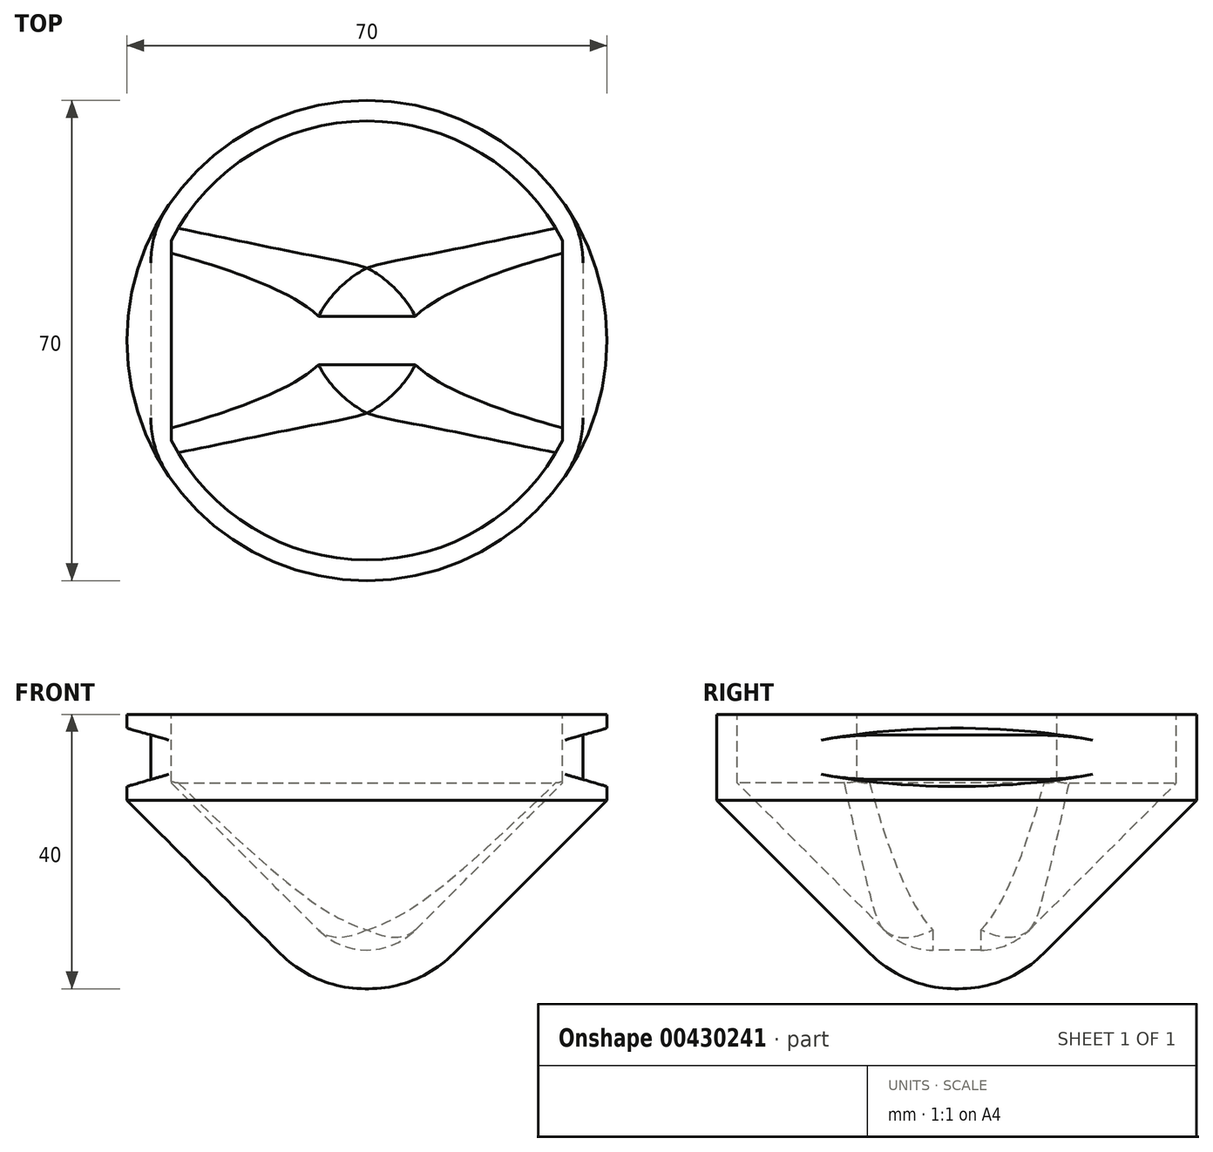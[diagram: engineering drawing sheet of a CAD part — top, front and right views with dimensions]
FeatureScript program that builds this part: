
annotation { "Feature Type Name" : "Feature", "Feature Type Description" : "" }
export const myFeature = defineFeature(function(context is Context, id is Id, definition is map)
    precondition{}
    {
        {
            var Q0;
            Q0=qCreatedBy(makeId("Top.planeOp"),FACE);
            var sketch = newSketch(context, id + "F0", { "sketchPlane" : qUnion([Q0])});
            skCircle(sketch, "E0", {"center": v(0, 0) * mm, "radius": 35 * mm});
            skSolve(sketch);
        }
        {
            var Q0;
            Q0=qSketchRegion(id+"F0",true);
            extrude(context, id + "F1", {"entities" : qUnion([Q0]), "depth" : 12.5 * mm});
        }
        {
            var Q0;
            Q0=makeQuery(id+"F1.opExtrude","CAP_FACE",FACE,{"disambiguationData":[OSD([sQuery(id+"F0.wireOp",EDGE,"E0")])],"isStart":false});
            var sketch = newSketch(context, id + "F2", { "sketchPlane" : qUnion([Q0])});
            skCircle(sketch, "E1", {"center": v(0, 0) * mm, "radius": 34 * mm});
            skSolve(sketch);
        }
        {
            var Q0;
            Q0=qSketchRegion(id+"F2",true);
            var Q1;
            Q1=makeQuery(id+"F1.opExtrude","CAP_FACE",FACE,{"disambiguationData":[OSD([sQuery(id+"F0.wireOp",EDGE,"E0")])],"isStart":true});
            extrude(context, id + "F3", {"entities" : qUnion([Q0]), "operationType" : NewBodyOperationType.ADD, "endBound" : BoundingType.UP_TO_SURFACE, "oppositeDirection" : true, "endBoundEntityFace" : qUnion([Q1]), "depth" : 25 * mm});
        }
        {
            var Q0;
            Q0=qCreatedBy(makeId("Front.planeOp"),FACE);
            var sketch = newSketch(context, id + "F4", { "sketchPlane" : qUnion([Q0])});
            skLineSegment(sketch, "E2", {"start": v(-35, 10.5) * mm, "end": v(-35, 2) * mm});
            skLineSegment(sketch, "E3", {"start": v(-35, 2) * mm, "end": v(-31.5, 3) * mm});
            skLineSegment(sketch, "E4", {"start": v(-31.5, 3) * mm, "end": v(-31.5, 9.5) * mm});
            skLineSegment(sketch, "E5", {"start": v(-31.5, 9.5) * mm, "end": v(-35, 10.5) * mm});
            skLineSegment(sketch, "E6.MirrorCS", {"start": v(35, 10.5) * mm, "end": v(35, 2) * mm});
            skLineSegment(sketch, "E7.MirrorCS", {"start": v(31.5, 9.5) * mm, "end": v(35, 10.5) * mm});
            skLineSegment(sketch, "E8.MirrorCS", {"start": v(35, 2) * mm, "end": v(31.5, 3) * mm});
            skLineSegment(sketch, "E9.MirrorCS", {"start": v(31.5, 3) * mm, "end": v(31.5, 9.5) * mm});
            skSolve(sketch);
        }
        {
            var Q0;
            Q0=qSketchRegion(id+"F4",true);
            extrude(context, id + "F5", {"entities" : qUnion([Q0]), "operationType" : NewBodyOperationType.REMOVE, "endBound" : BoundingType.THROUGH_ALL, "oppositeDirection" : true, "depth" : 25 * mm, "hasSecondDirection" : true, "secondDirectionBound" : SecondDirectionBoundingType.THROUGH_ALL, "secondDirectionOppositeDirection" : false, "secondDirectionDepth" : 25 * mm});
        }
        {
            var Q0;
            {var subQ0=sQuery(id+"F0.wireOp",EDGE,"E0");Q0=makeQuery(id+"F5.boolean.opBoolean","INTERSECT",EDGE,{"disambiguationData":[OD(0.0)],"derivedFrom":[makeQuery(id+"FLbTWpatOgGcuB9_1.boolean.opBoolean","SPLIT",FACE,{"disambiguationData":[TD([makeQuery(id+"F1.opExtrude","CAP_FACE",FACE,{"disambiguationData":[OSD([subQ0])],"isStart":true})])],"derivedFrom":makeQuery(id+"F1.opExtrude","SWEPT_FACE",FACE,{"disambiguationData":[OSD([subQ0])]})}),makeQuery(id+"F5.opExtrude","SWEPT_FACE",FACE,{"disambiguationData":[OSD([sQuery(id+"F4.wireOp",EDGE,"E4")])]})]});}
            var Q1;
            {var subQ0=sQuery(id+"F0.wireOp",EDGE,"E0");Q1=makeQuery(id+"F5.boolean.opBoolean","INTERSECT",EDGE,{"disambiguationData":[OD(0.0)],"derivedFrom":[makeQuery(id+"FLbTWpatOgGcuB9_1.boolean.opBoolean","SPLIT",FACE,{"disambiguationData":[TD([makeQuery(id+"F1.opExtrude","CAP_FACE",FACE,{"disambiguationData":[OSD([subQ0])],"isStart":true})])],"derivedFrom":makeQuery(id+"F1.opExtrude","SWEPT_FACE",FACE,{"disambiguationData":[OSD([subQ0])]})}),makeQuery(id+"F5.opExtrude","SWEPT_FACE",FACE,{"disambiguationData":[OSD([sQuery(id+"F4.wireOp",EDGE,"E9.MirrorCS")])]})]});}
            var Q2;
            {var subQ0=sQuery(id+"F0.wireOp",EDGE,"E0");Q2=makeQuery(id+"F5.boolean.opBoolean","INTERSECT",EDGE,{"disambiguationData":[OD(1.0)],"derivedFrom":[makeQuery(id+"FLbTWpatOgGcuB9_1.boolean.opBoolean","SPLIT",FACE,{"disambiguationData":[TD([makeQuery(id+"F1.opExtrude","CAP_FACE",FACE,{"disambiguationData":[OSD([subQ0])],"isStart":true})])],"derivedFrom":makeQuery(id+"F1.opExtrude","SWEPT_FACE",FACE,{"disambiguationData":[OSD([subQ0])]})}),makeQuery(id+"F5.opExtrude","SWEPT_FACE",FACE,{"disambiguationData":[OSD([sQuery(id+"F4.wireOp",EDGE,"E9.MirrorCS")])]})]});}
            var Q3;
            {var subQ0=sQuery(id+"F0.wireOp",EDGE,"E0");Q3=makeQuery(id+"F5.boolean.opBoolean","INTERSECT",EDGE,{"disambiguationData":[OD(1.0)],"derivedFrom":[makeQuery(id+"FLbTWpatOgGcuB9_1.boolean.opBoolean","SPLIT",FACE,{"disambiguationData":[TD([makeQuery(id+"F1.opExtrude","CAP_FACE",FACE,{"disambiguationData":[OSD([subQ0])],"isStart":true})])],"derivedFrom":makeQuery(id+"F1.opExtrude","SWEPT_FACE",FACE,{"disambiguationData":[OSD([subQ0])]})}),makeQuery(id+"F5.opExtrude","SWEPT_FACE",FACE,{"disambiguationData":[OSD([sQuery(id+"F4.wireOp",EDGE,"E4")])]})]});}
            fillet(context, id + "F6", {"entities" : qUnion([Q0, Q1, Q2, Q3]), "radius" : 15 * mm, "tangentPropagation" : true, "allowEdgeOverflow" : false});
        }
        {
            var Q0;
            Q0=makeQuery(id+"F1.opExtrude","CAP_FACE",FACE,{"disambiguationData":[OSD([sQuery(id+"F0.wireOp",EDGE,"E0")])],"isStart":true});
            var sketch = newSketch(context, id + "F7", { "sketchPlane" : qUnion([Q0])});
            skCircle(sketch, "E10.0.0", {"center": v(0, 0) * mm, "radius": 35 * mm});
            skSolve(sketch);
        }
        {
            var Q0;
            Q0=qSketchRegion(id+"F7",true);
            extrude(context, id + "F8", {"entities" : qUnion([Q0]), "operationType" : NewBodyOperationType.ADD, "depth" : 27.5 * mm, "hasDraft" : true, "draftAngle" : 45 * degree, "draftPullDirection" : true});
        }
        {
            var Q0;
            Q0=makeQuery(id+"F1.opExtrude","CAP_FACE",FACE,{"disambiguationData":[OSD([sQuery(id+"F0.wireOp",EDGE,"E0")])],"isStart":false});
            var sketch = newSketch(context, id + "F9", { "sketchPlane" : qUnion([Q0])});
            skArc(sketch, "E11", {"start": v(-28.5, -14.55) * mm, "mid": v(0, -32) * mm, "end": v(28.5, -14.55) * mm});
            skLineSegment(sketch, "E12", {"start": v(-28.5, 14.55) * mm, "end": v(-28.5, -14.55) * mm});
            skLineSegment(sketch, "E13", {"start": v(28.5, 14.55) * mm, "end": v(28.5, -14.55) * mm});
            skArc(sketch, "E14.trimOffspring", {"start": v(28.5, 14.55) * mm, "mid": v(0, 32) * mm, "end": v(-28.5, 14.55) * mm});
            skSolve(sketch);
        }
        {
            var Q0;
            Q0=qSketchRegion(id+"F9",true);
            extrude(context, id + "F10", {"entities" : qUnion([Q0]), "operationType" : NewBodyOperationType.REMOVE, "oppositeDirection" : true, "depth" : 10 * mm});
        }
        {
            var Q0;
            Q0=makeQuery(id+"F10.boolean.opBoolean","COPY",FACE,{"derivedFrom":makeQuery(id+"F10.opExtrude","CAP_FACE",FACE,{"disambiguationData":[OSD([sQuery(id+"F9.wireOp",EDGE,"E11"),sQuery(id+"F9.wireOp",EDGE,"E12"),sQuery(id+"F9.wireOp",EDGE,"E13"),sQuery(id+"F9.wireOp",EDGE,"E14.trimOffspring")])],"isStart":false})});
            var sketch = newSketch(context, id + "F11", { "sketchPlane" : qUnion([Q0])});
            skArc(sketch, "E15.0", {"start": v(28.5, 14.55) * mm, "mid": v(0, 32) * mm, "end": v(-28.5, 14.55) * mm});
            skLineSegment(sketch, "E16.0", {"start": v(-28.5, 14.55) * mm, "end": v(-28.5, -14.55) * mm});
            skArc(sketch, "E16.1", {"start": v(-28.5, -14.55) * mm, "mid": v(0, -32) * mm, "end": v(28.5, -14.55) * mm});
            skLineSegment(sketch, "E16.2", {"start": v(28.5, 14.55) * mm, "end": v(28.5, -14.55) * mm});
            skSolve(sketch);
        }
        {
            var Q0;
            Q0=qSketchRegion(id+"F11",true);
            extrude(context, id + "F12", {"entities" : qUnion([Q0]), "operationType" : NewBodyOperationType.REMOVE, "endBound" : BoundingType.THROUGH_ALL, "oppositeDirection" : true, "depth" : 45 * mm, "hasDraft" : true, "draftAngle" : 45 * degree, "draftPullDirection" : true});
        }
        {
            var Q0;
            Q0=makeQuery(id+"F12.boolean.opBoolean","COPY",EDGE,{"derivedFrom":makeQuery(id+"F12.*.draft.opDraft","SPLIT",EDGE,{"derivedFrom":makeQuery(id+"F12.opExtrude","SWEPT_EDGE",EDGE,{"disambiguationData":[OSD([sQuery(id+"F11.wireOp",EDGE,"E15.0"),sQuery(id+"F11.wireOp",EDGE,"E16.0")])]})})});
            var Q1;
            {var subQ0=sQuery(id+"F11.wireOp",EDGE,"E16.2");var subQ1=sQuery(id+"F11.wireOp",EDGE,"E15.0");var subQ2=sQuery(id+"F11.wireOp",EDGE,"E16.0");var subQ3=sQuery(id+"F11.wireOp",EDGE,"E16.1");Q1=makeQuery(id+"F12.boolean.opBoolean","COPY",EDGE,{"derivedFrom":makeQuery(id+"F12.*.draft.opDraft","MERGE",EDGE,{"derivedFrom":[makeQuery(id+"F12.opExtrude","SWEPT_EDGE",EDGE,{"disambiguationData":[OSD([subQ2,subQ3])]}),makeQuery(id+"F12.opExtrude","SWEPT_EDGE",EDGE,{"disambiguationData":[OSD([subQ3,subQ0])]}),makeQuery(id+"F12.opExtrude","SWEPT_EDGE",EDGE,{"disambiguationData":[OSD([subQ1,subQ2])]}),makeQuery(id+"F12.opExtrude","SWEPT_EDGE",EDGE,{"disambiguationData":[OSD([subQ1,subQ0])]})]})});}
            var Q2;
            Q2=makeQuery(id+"F12.boolean.opBoolean","COPY",EDGE,{"derivedFrom":makeQuery(id+"F12.*.draft.opDraft","SPLIT",EDGE,{"derivedFrom":makeQuery(id+"F12.opExtrude","SWEPT_EDGE",EDGE,{"disambiguationData":[OSD([sQuery(id+"F11.wireOp",EDGE,"E15.0"),sQuery(id+"F11.wireOp",EDGE,"E16.2")])]})})});
            var Q3;
            Q3=makeQuery(id+"F12.boolean.opBoolean","COPY",EDGE,{"derivedFrom":makeQuery(id+"F12.*.draft.opDraft","SPLIT",EDGE,{"derivedFrom":makeQuery(id+"F12.opExtrude","SWEPT_EDGE",EDGE,{"disambiguationData":[OSD([sQuery(id+"F11.wireOp",EDGE,"E16.1"),sQuery(id+"F11.wireOp",EDGE,"E16.2")])]})})});
            var Q4;
            Q4=makeQuery(id+"F12.boolean.opBoolean","COPY",EDGE,{"derivedFrom":makeQuery(id+"F12.*.draft.opDraft","SPLIT",EDGE,{"derivedFrom":makeQuery(id+"F12.opExtrude","SWEPT_EDGE",EDGE,{"disambiguationData":[OSD([sQuery(id+"F11.wireOp",EDGE,"E16.0"),sQuery(id+"F11.wireOp",EDGE,"E16.1")])]})})});
            fillet(context, id + "F13", {"entities" : qUnion([Q0, Q1, Q2, Q3, Q4]), "radius" : 10 * mm, "allowEdgeOverflow" : false});
        }
        {
            var Q0;
            Q0=makeQuery(id+"F8.opExtrude","CAP_EDGE",EDGE,{"disambiguationData":[OSD([sQuery(id+"F7.wireOp",EDGE,"E10.0.0")])],"isStart":false});
            fillet(context, id + "F14", {"entities" : qUnion([Q0]), "radius" : 17.5 * mm, "tangentPropagation" : true, "allowEdgeOverflow" : false});
        }
    });
